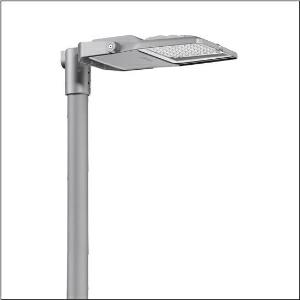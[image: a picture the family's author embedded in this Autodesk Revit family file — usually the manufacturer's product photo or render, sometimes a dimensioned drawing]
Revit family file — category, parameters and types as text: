
# Revit family: floodlight_fl_21_iq_mini___pl52_5xa7772b2d3a_55c6
name_source: partatom
category: Lighting Fixtures
units: mm (PartAtom-declared; Revit-internal decimal feet)

## family parameters
Cut with Voids When Loaded = No
Host = Face
Light Source = No
Part Type = Normal
Room Calculation Point = No
Round Connector Dimension = Use Diameter
Shared = No

## types (1)
- --- (1 x LED, 6240 lm, 45.5 W, 3000K)
    Apparent Load = 46 VA
    CIE Flux Codes = 26 60 98 100 100
    Color Rendering = 70
    Color Temperature = 3000K
    Default Elevation = 1800 mm
    Description = Floodlight FL 21 iQ mini, floodlight, primary light control with lens, of PMMA, primary optical cover: protective disc, of toughened safety glass, transparent, light distribution: PL52, light emission: direct distribution, installation type: surface-mounted, LED, High Power LED, rated luminous flux: 6.240lm, luminous efficacy: 137lm/W, light colour: 730, colour temperature: 3000K, control: Auto-Match, Temp-Guard, Night-Set, Smart-Wire, Desk-Remote (wireless, voltage-free reading and setting of iQ features in the workshop via application-optimized NFC function/RFID function), optimised constant luminous flux control (CLO 2.0), Light-Fading, Lumen-Switch, with terminal, 6-pole, mains connection: 220..240V, AC, 50/60Hz, start of lifetime: 46W, end of service life: 48W, reduction: 22W, luminaire housing, of diecast aluminium, powder-coated, Siteco® metallic grey (DB 702S), corrosivity category C5 mid according to DIN EN ISO 12944, sealing non-destructively replaceable, please order mast flange separately, mast bracket, of steel, galvanised, powder-coated, protection rating (complete): IP66, insulation class (complete): insulation class II (safety insulation), certification: CE, ENEC, VDE, protection symbol: D, impact resistance: IK08, permissible operating ambient temperature: -40..+40°C, permissible operating ambient temperature for outdoor applications: -40..+50°C, standard: DIN EN 12944, LABS conformity tested according to VDMA 24364:2018-05, packaging unit: 1 piece

Light Distribution: PL52
    Height = 70 mm
    Lamp = 1 x LED
    Lamp Light Flux = 6240 lm
    Lamp Power = 45.5 W
    Lamp count = 1
    Length = 485 mm
    Luminous efficacy = 137 lm/W
    Manufacturer = Siteco
    ModVariant = No
    Model = 5XA7772B2D3A
    Number of Poles = 1
    OnlyDefault = Yes
    Power Factor = 1
    Product Name = Floodlight FL 21 iQ mini | PL52
    Product group = floodlight | pylon annexe
    ProductGroupID = 6200
    Protection Class = Protection class II
    Protection Degree = IP 66
    RLX_Detail_Level = 1
    RLX_Emergency_Light_Flux = 0 lm
    RLX_Emergency_Type = 0
    RLX_Emergency_Type_DB = No
    RlxData = <blob elided: 101421 chars, md5=259c44e1>
    Socket = socket
    Standby Power = 0 W
    System Light Flux = 6240 lm
    System Power = 46 W
    Type Comments = factory setting: luminous flux: 100 % | dim-lin: 254 | 463 mA
    Type Image = l_1007125.jpg
    URL = http://relux.com
    VarID = @adj_114995
    Voltage = 0 V
    Weight = 0.00 kg
    Width = 337 mm

## geometry (parser evidence)
native form markers: Blend x4, Sweep x13
no freeform markers — native parametric forms only
